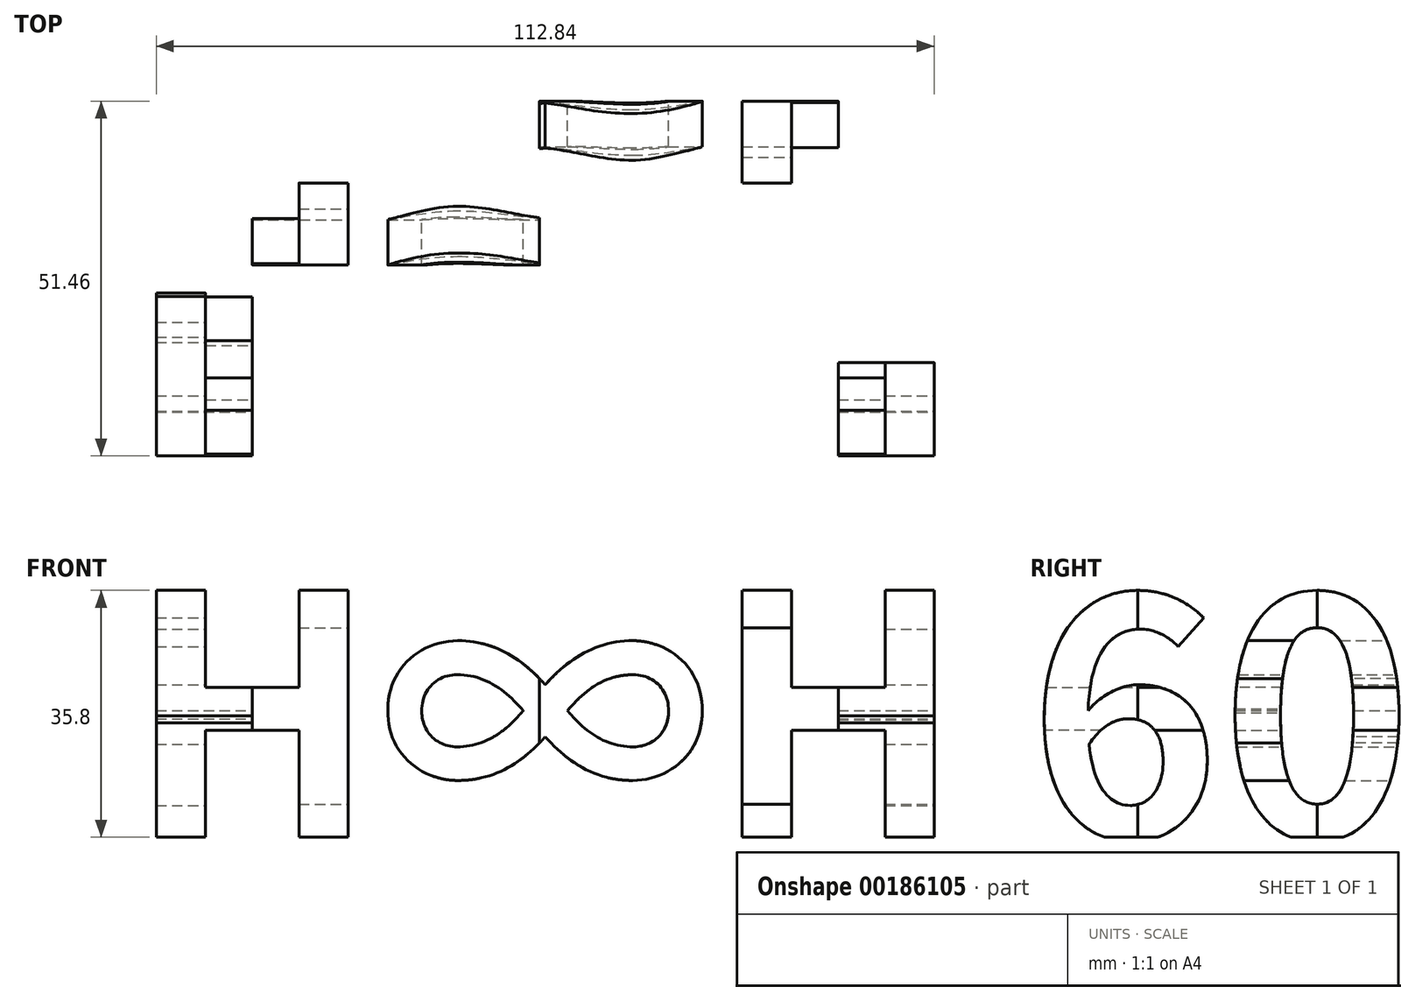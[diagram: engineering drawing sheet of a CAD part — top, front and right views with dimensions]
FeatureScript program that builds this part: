
annotation { "Feature Type Name" : "Feature", "Feature Type Description" : "" }
export const myFeature = defineFeature(function(context is Context, id is Id, definition is map)
    precondition{}
    {
        {
            var Q0;
            Q0=qCreatedBy(makeId("Front.planeOp"),FACE);
            var sketch = newSketch(context, id + "F0", { "sketchPlane" : qUnion([Q0])});
            skText(sketch, "E0", { "text": "H∞H", "fontName": "NotoSansCJKsc-Bold.otf"});
            const initialGuessF0  = {"E0": [-0.06, 0, 1, 0, 0.03484]};
            skSetInitialGuess(sketch, initialGuessF0);
            skSolve(sketch);
        }
        {
            var Q0;
            Q0 = qSketchRegion(id + "F0", true);
            extrude(context, id + "F1", {"entities" : qUnion([Q0]), "depth" : 50 * mm, "hasSecondDirection" : true, "secondDirectionOppositeDirection" : true, "secondDirectionDepth" : 50 * mm});
        }
        {
            var Q0;
            Q0=qCreatedBy(makeId("Right.planeOp"),FACE);
            var sketch = newSketch(context, id + "F2", { "sketchPlane" : qUnion([Q0])});
            skText(sketch, "E1", { "text": "60", "fontName": "NotoSansCJKsc-Bold.otf"});
            const initialGuessF2  = {"E1": [-0.02827, 0, 1, 0, 0.03418]};
            skSetInitialGuess(sketch, initialGuessF2);
            skSolve(sketch);
        }
        {
            var Q0;
            Q0 = qSketchRegion(id + "F2", true);
            extrude(context, id + "F3", {"entities" : qUnion([Q0]), "operationType" : NewBodyOperationType.INTERSECT, "endBound" : BoundingType.THROUGH_ALL, "oppositeDirection" : true, "depth" : 25 * mm, "hasSecondDirection" : true, "secondDirectionBound" : SecondDirectionBoundingType.THROUGH_ALL, "secondDirectionOppositeDirection" : false, "secondDirectionDepth" : 25 * mm});
        }
        {
            var Q0;
            Q0=qCreatedBy(makeId("Top.planeOp"),FACE);
            var sketch = newSketch(context, id + "F4", { "sketchPlane" : qUnion([Q0])});
            skLineSegment(sketch, "E2.bottom", {"start": v(0, 0) * mm, "end": v(-22.01, 0) * mm});
            skLineSegment(sketch, "E2.top", {"start": v(0, 10.35) * mm, "end": v(-22.01, 10.35) * mm});
            skLineSegment(sketch, "E2.left", {"start": v(0, 0) * mm, "end": v(0, 10.35) * mm});
            skLineSegment(sketch, "E2.right", {"start": v(-22.01, 0) * mm, "end": v(-22.01, 10.35) * mm});
            skLineSegment(sketch, "E3.bottom", {"start": v(0, 17.02) * mm, "end": v(23.62, 17.02) * mm});
            skLineSegment(sketch, "E3.top", {"start": v(0, 25.57) * mm, "end": v(23.62, 25.57) * mm});
            skLineSegment(sketch, "E3.left", {"start": v(0, 17.02) * mm, "end": v(0, 25.57) * mm});
            skLineSegment(sketch, "E3.right", {"start": v(23.62, 17.02) * mm, "end": v(23.62, 25.57) * mm});
            skLineSegment(sketch, "E4.bottom", {"start": v(-55.6, -25.9) * mm, "end": v(-41.66, -25.9) * mm});
            skLineSegment(sketch, "E4.top", {"start": v(-55.6, -2.25) * mm, "end": v(-41.66, -2.25) * mm});
            skLineSegment(sketch, "E4.left", {"start": v(-55.6, -25.9) * mm, "end": v(-55.6, -2.25) * mm});
            skLineSegment(sketch, "E4.right", {"start": v(-41.66, -25.9) * mm, "end": v(-41.66, -2.25) * mm});
            skLineSegment(sketch, "E5.bottom", {"start": v(-41.66, 13.7) * mm, "end": v(-27.77, 13.7) * mm});
            skLineSegment(sketch, "E5.top", {"start": v(-41.66, 0) * mm, "end": v(-27.77, 0) * mm});
            skLineSegment(sketch, "E5.left", {"start": v(-41.66, 13.7) * mm, "end": v(-41.66, 0) * mm});
            skLineSegment(sketch, "E5.right", {"start": v(-27.77, 13.7) * mm, "end": v(-27.77, 0) * mm});
            skLineSegment(sketch, "E6.bottom", {"start": v(43.34, 13.7) * mm, "end": v(29.43, 13.7) * mm});
            skLineSegment(sketch, "E6.top", {"start": v(43.34, 25.57) * mm, "end": v(29.43, 25.57) * mm});
            skLineSegment(sketch, "E6.left", {"start": v(29.43, 13.7) * mm, "end": v(29.43, 25.57) * mm});
            skLineSegment(sketch, "E6.right", {"start": v(43.34, 13.7) * mm, "end": v(43.34, 25.57) * mm});
            skLineSegment(sketch, "E7.bottom", {"start": v(57.26, -25.9) * mm, "end": v(43.34, -25.9) * mm});
            skLineSegment(sketch, "E7.top", {"start": v(57.26, -12.32) * mm, "end": v(43.34, -12.32) * mm});
            skLineSegment(sketch, "E7.left", {"start": v(57.26, -25.9) * mm, "end": v(57.26, -12.32) * mm});
            skLineSegment(sketch, "E7.right", {"start": v(43.34, -25.9) * mm, "end": v(43.34, -12.32) * mm});
            skSolve(sketch);
        }
        {
            var Q0;
            Q0 = qSketchRegion(id + "F4", true);
            extrude(context, id + "F5", {"entities" : qUnion([Q0]), "operationType" : NewBodyOperationType.INTERSECT, "endBound" : BoundingType.THROUGH_ALL, "depth" : 25 * mm});
        }
    });
